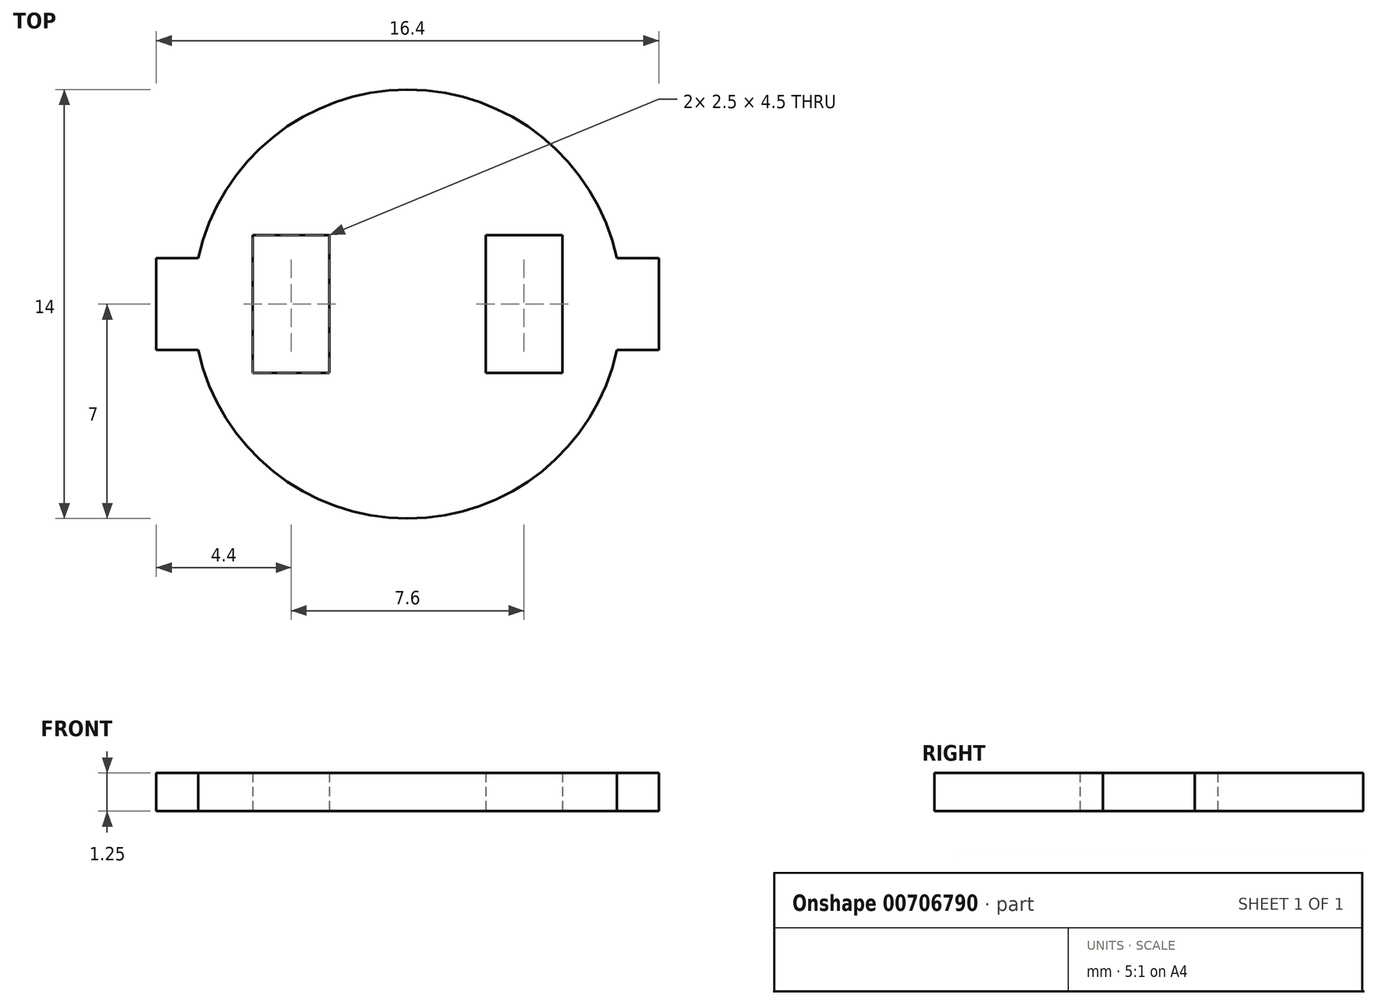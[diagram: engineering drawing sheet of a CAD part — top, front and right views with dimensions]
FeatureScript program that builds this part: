
annotation { "Feature Type Name" : "Feature", "Feature Type Description" : "" }
export const myFeature = defineFeature(function(context is Context, id is Id, definition is map)
    precondition{}
    {
        {
            var Q0;
            Q0=qCreatedBy(makeId("Top.planeOp"),FACE);
            var sketch = newSketch(context, id + "F0", { "sketchPlane" : qUnion([Q0])});
            skArc(sketch, "E0", {"start": v(6.84, 1.5) * mm, "mid": v(0, 7) * mm, "end": v(-6.84, 1.5) * mm});
            skLineSegment(sketch, "E1", {"start": v(-6.84, 1.5) * mm, "end": v(-8.2, 1.5) * mm});
            skLineSegment(sketch, "E2", {"start": v(-8.2, 1.5) * mm, "end": v(-8.2, -1.5) * mm});
            skLineSegment(sketch, "E3", {"start": v(-8.2, -1.5) * mm, "end": v(-6.84, -1.5) * mm});
            skLineSegment(sketch, "E4.MirrorCS", {"start": v(6.84, 1.5) * mm, "end": v(8.2, 1.5) * mm});
            skLineSegment(sketch, "E5.MirrorCS", {"start": v(8.2, -1.5) * mm, "end": v(6.84, -1.5) * mm});
            skLineSegment(sketch, "E6.MirrorCS", {"start": v(8.2, 1.5) * mm, "end": v(8.2, -1.5) * mm});
            skArc(sketch, "E7.trimOffspring", {"start": v(-6.84, -1.5) * mm, "mid": v(0, -7) * mm, "end": v(6.84, -1.5) * mm});
            skLineSegment(sketch, "E8.bottom", {"start": v(-5.05, 2.25) * mm, "end": v(-2.55, 2.25) * mm});
            skLineSegment(sketch, "E8.top", {"start": v(-5.05, -2.25) * mm, "end": v(-2.55, -2.25) * mm});
            skLineSegment(sketch, "E8.left", {"start": v(-5.05, 2.25) * mm, "end": v(-5.05, -2.25) * mm});
            skLineSegment(sketch, "E8.right", {"start": v(-2.55, 2.25) * mm, "end": v(-2.55, -2.25) * mm});
            skPoint(sketch, "E8.middle", {"position": v(-3.8, 0) * mm});
            skLineSegment(sketch, "E9.bottom", {"start": v(2.55, 2.25) * mm, "end": v(5.05, 2.25) * mm});
            skLineSegment(sketch, "E9.top", {"start": v(2.55, -2.25) * mm, "end": v(5.05, -2.25) * mm});
            skLineSegment(sketch, "E9.left", {"start": v(2.55, 2.25) * mm, "end": v(2.55, -2.25) * mm});
            skLineSegment(sketch, "E9.right", {"start": v(5.05, 2.25) * mm, "end": v(5.05, -2.25) * mm});
            skPoint(sketch, "E9.middle", {"position": v(3.8, 0) * mm});
            skSolve(sketch);
        }
        {
            var Q0;
            Q0=makeQuery(id+"F0.imprint","IMPRINT",FACE,{"disambiguationData":[TD([[makeQuery(id+"F0.imprint","IMPRINT",EDGE,{"derivedFrom":sQuery(id+"F0.wireOp",EDGE,"E0")}),1.0]])]});
            extrude(context, id + "F1", {"entities" : qUnion([Q0]), "depth" : 1.25 * mm, "offsetDistance" : 25 * mm});
        }
    });
